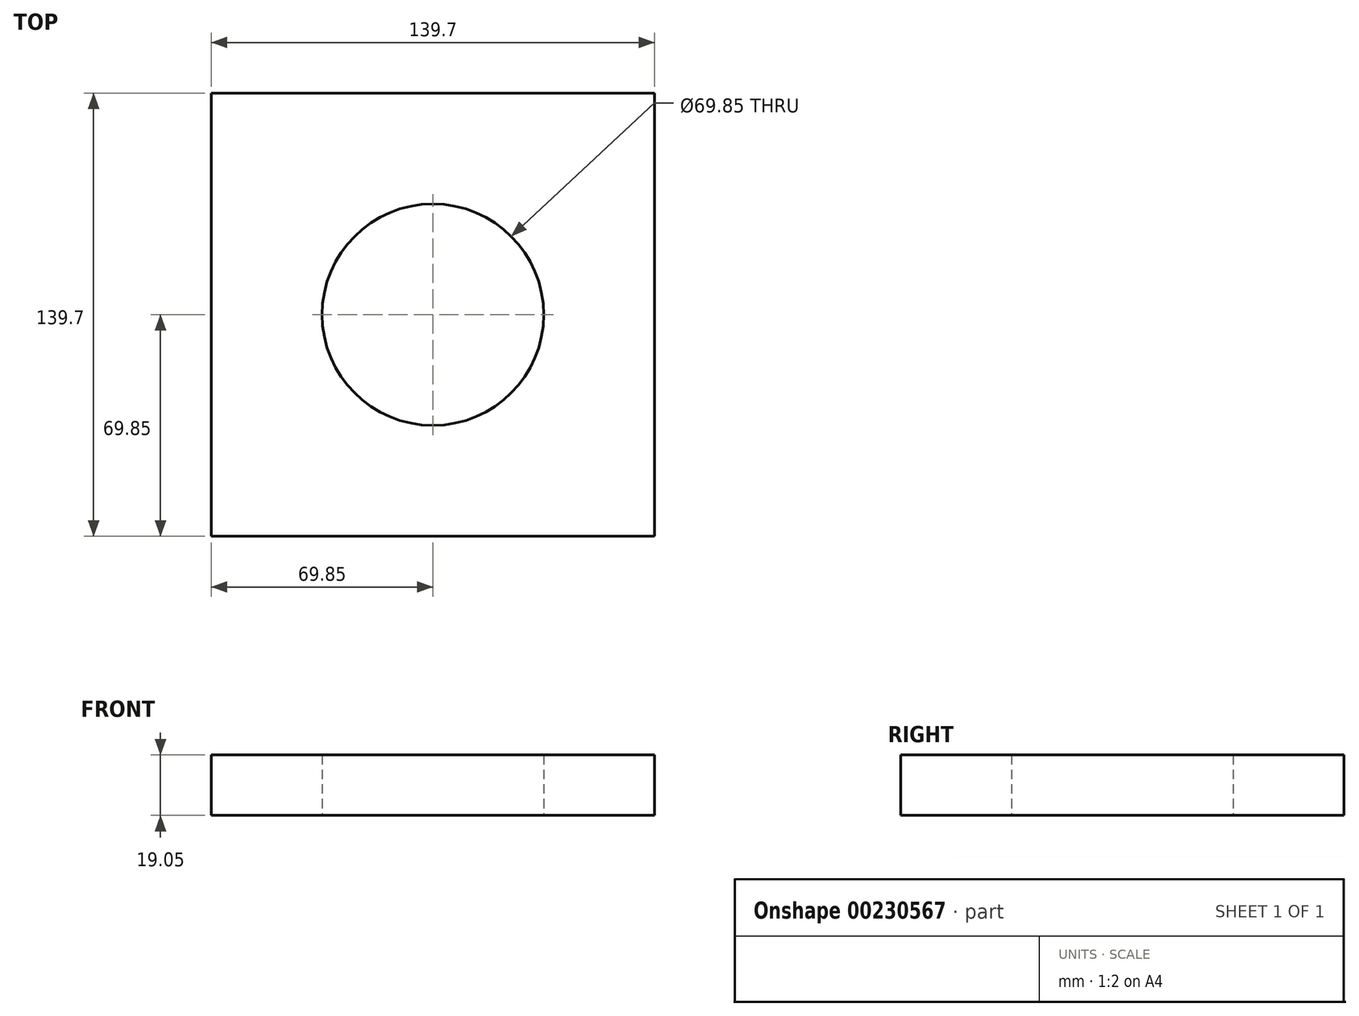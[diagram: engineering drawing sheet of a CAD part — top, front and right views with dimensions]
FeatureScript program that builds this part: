
annotation { "Feature Type Name" : "Feature", "Feature Type Description" : "" }
export const myFeature = defineFeature(function(context is Context, id is Id, definition is map)
    precondition{}
    {
        {
            var Q0;
            Q0=qCreatedBy(makeId("Top.planeOp"),FACE);
            var sketch = newSketch(context, id + "F0", { "sketchPlane" : qUnion([Q0])});
            skLineSegment(sketch, "E0.bottom", {"start": v(69.85, 69.85) * mm, "end": v(-69.85, 69.85) * mm});
            skLineSegment(sketch, "E0.top", {"start": v(69.85, -69.85) * mm, "end": v(-69.85, -69.85) * mm});
            skLineSegment(sketch, "E0.left", {"start": v(69.85, 69.85) * mm, "end": v(69.85, -69.85) * mm});
            skLineSegment(sketch, "E0.right", {"start": v(-69.85, 69.85) * mm, "end": v(-69.85, -69.85) * mm});
            skPoint(sketch, "E0.middle", {"position": v(0, 0) * mm});
            skCircle(sketch, "E1", {"center": v(0, 0) * mm, "radius": 34.93 * mm});
            skSolve(sketch);
        }
        {
            var Q0;
            Q0 = qSketchRegion(id + "F0", true);
            extrude(context, id + "F1", {"entities" : qUnion([Q0]), "depth" : 19.05 * mm});
        }
    });
